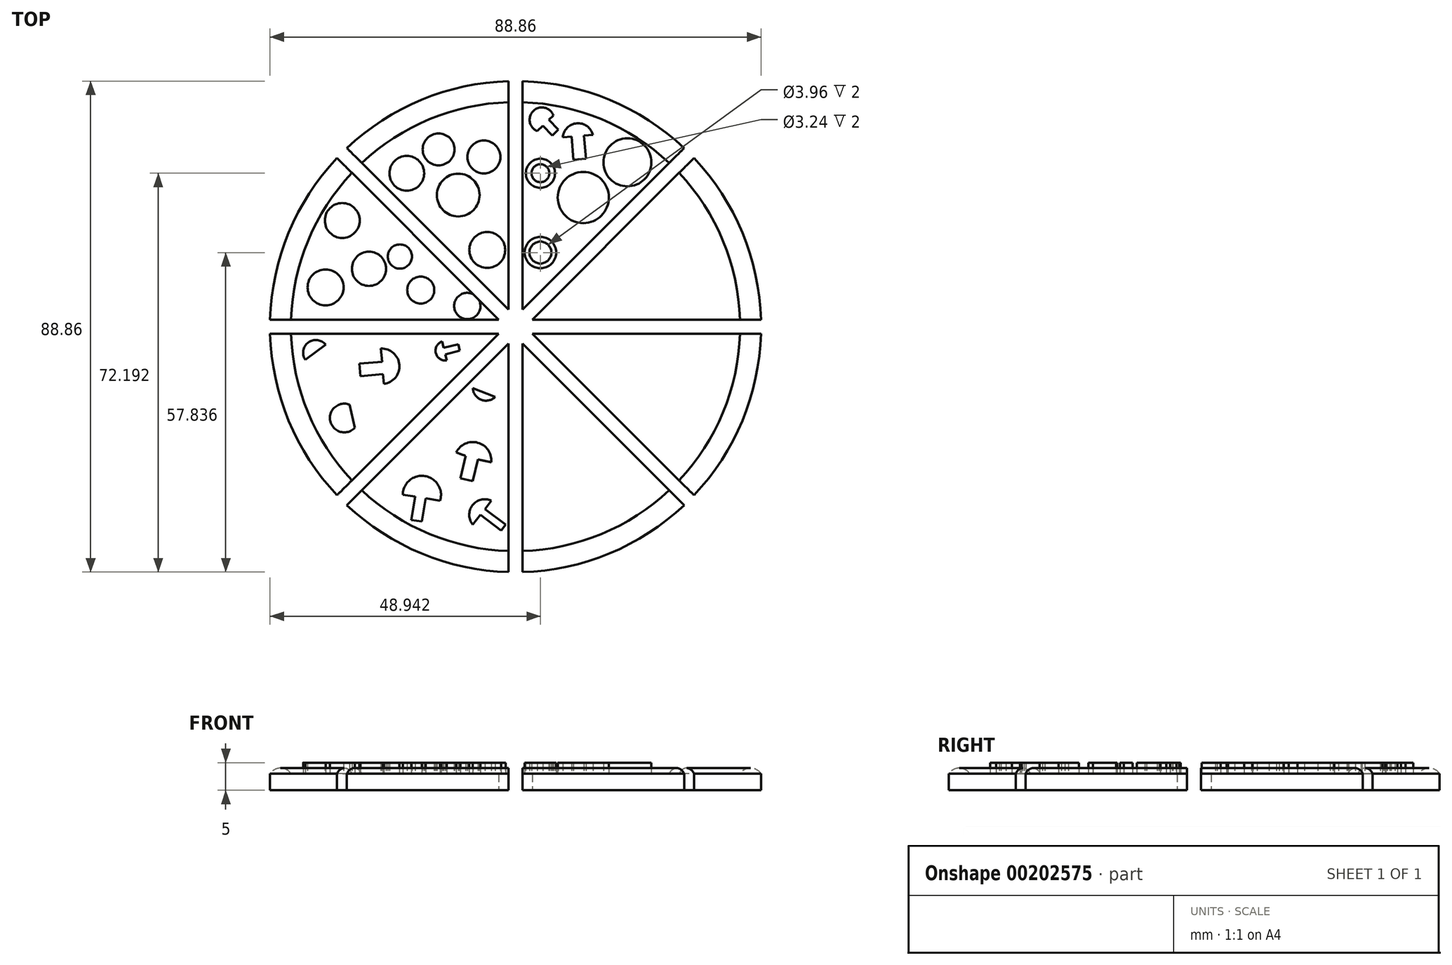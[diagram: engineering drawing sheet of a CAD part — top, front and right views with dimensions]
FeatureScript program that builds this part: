
annotation { "Feature Type Name" : "Feature", "Feature Type Description" : "" }
export const myFeature = defineFeature(function(context is Context, id is Id, definition is map)
    precondition{}
    {
        {
            var Q0;
            Q0=qCreatedBy(makeId("Top.planeOp"),FACE);
            var sketch = newSketch(context, id + "F0", { "sketchPlane" : qUnion([Q0])});
            skCircle(sketch, "E0", {"center": v(0, 0) * mm, "radius": 44.45 * mm});
            skSolve(sketch);
        }
        {
            var Q0;
            Q0 = qSketchRegion(id + "F0", true);
            extrude(context, id + "F1", {"entities" : qUnion([Q0]), "depth" : 2 * mm});
        }
        {
            var Q0;
            Q0=makeQuery(id+"F1.opExtrude","CAP_FACE",FACE,{"disambiguationData":[OSD([sQuery(id+"F0.wireOp",EDGE,"E0")])],"isStart":false});
            var sketch = newSketch(context, id + "F2", { "sketchPlane" : qUnion([Q0])});
            skLineSegment(sketch, "E1", {"start": v(0, 0) * mm, "end": v(0, 44.45) * mm});
            skLineSegment(sketch, "E2", {"start": v(0, 44.45) * mm, "end": v(0, -44.45) * mm});
            skLineSegment(sketch, "E3", {"start": v(0, -44.45) * mm, "end": v(0, 0) * mm});
            skLineSegment(sketch, "E4", {"start": v(0, 0) * mm, "end": v(-44.45, 0) * mm});
            skLineSegment(sketch, "E5", {"start": v(0, 0) * mm, "end": v(44.45, 0) * mm});
            skLineSegment(sketch, "E6", {"start": v(0, 0) * mm, "end": v(-31.43, -31.43) * mm});
            skLineSegment(sketch, "E7", {"start": v(-31.43, -31.43) * mm, "end": v(31.43, 31.43) * mm});
            skLineSegment(sketch, "E8", {"start": v(31.43, 31.43) * mm, "end": v(0, 0) * mm});
            skLineSegment(sketch, "E9", {"start": v(0, 0) * mm, "end": v(-31.43, 31.43) * mm});
            skLineSegment(sketch, "E10", {"start": v(0, 0) * mm, "end": v(31.43, -31.43) * mm});
            skSolve(sketch);
        }
        {
            var Q0;
            {var subQ0=sQuery(id+"F2.wireOp",EDGE,"E4");Q0=makeQuery(id+"F2.imprint","IMPRINT",FACE,{"disambiguationData":[TD([[makeQuery(id+"F2.imprint","IMPRINT",EDGE,{"derivedFrom":subQ0}),-1.0]])]});}
            var sketch = newSketch(context, id + "F3", { "sketchPlane" : qUnion([Q0])});
            skCircle(sketch, "E11", {"center": v(-17.15, 6.62) * mm, "radius": 2.44 * mm});
            skCircle(sketch, "E12", {"center": v(-26.52, 10.46) * mm, "radius": 3.1 * mm});
            skCircle(sketch, "E13", {"center": v(-34.38, 7.1) * mm, "radius": 3.26 * mm});
            skCircle(sketch, "E14", {"center": v(-31.36, 19.2) * mm, "radius": 3.15 * mm});
            skCircle(sketch, "E15", {"center": v(-20.94, 12.69) * mm, "radius": 2.19 * mm});
            skCircle(sketch, "E16", {"center": v(-8.72, 3.73) * mm, "radius": 2.38 * mm});
            skCircle(sketch, "E17", {"center": v(-5.1, 13.87) * mm, "radius": 3.25 * mm});
            skCircle(sketch, "E18", {"center": v(-10.37, 23.81) * mm, "radius": 3.87 * mm});
            skCircle(sketch, "E19", {"center": v(-19.68, 27.75) * mm, "radius": 3.14 * mm});
            skCircle(sketch, "E20", {"center": v(-5.73, 30.7) * mm, "radius": 2.98 * mm});
            skCircle(sketch, "E21", {"center": v(-13.92, 32.07) * mm, "radius": 2.88 * mm});
            skArc(sketch, "E22", {"start": v(-23.83, -10.37) * mm, "mid": v(-21.02, -6.92) * mm, "end": v(-24.36, -3.96) * mm});
            skLineSegment(sketch, "E23", {"start": v(-24.36, -3.96) * mm, "end": v(-23.83, -10.37) * mm});
            skLineSegment(sketch, "E24", {"start": v(-24.16, -6.4) * mm, "end": v(-28.23, -6.72) * mm});
            skLineSegment(sketch, "E25", {"start": v(-28.23, -6.72) * mm, "end": v(-28.04, -8.95) * mm});
            skLineSegment(sketch, "E26", {"start": v(-28.04, -8.95) * mm, "end": v(-23.83, -8.6) * mm});
            skArc(sketch, "E27", {"start": v(-30.03, -14.12) * mm, "mid": v(-33.53, -17.1) * mm, "end": v(-29.1, -18.34) * mm});
            skLineSegment(sketch, "E28", {"start": v(-30.03, -14.12) * mm, "end": v(-29.1, -18.34) * mm});
            skLineSegment(sketch, "E29", {"start": v(-29.75, -15.36) * mm, "end": v(-25.7, -14.84) * mm});
            skLineSegment(sketch, "E30", {"start": v(-25.66, -14.89) * mm, "end": v(-25.23, -16.85) * mm});
            skLineSegment(sketch, "E31", {"start": v(-25.28, -16.74) * mm, "end": v(-29.34, -17.23) * mm});
            skArc(sketch, "E32", {"start": v(-34.35, -3.28) * mm, "mid": v(-37.5, -2.87) * mm, "end": v(-38.06, -6) * mm});
            skLineSegment(sketch, "E33", {"start": v(-34.35, -3.28) * mm, "end": v(-38.06, -6) * mm});
            skLineSegment(sketch, "E34", {"start": v(-36.8, -5.08) * mm, "end": v(-34.95, -7.6) * mm});
            skLineSegment(sketch, "E35", {"start": v(-34.82, -7.51) * mm, "end": v(-33.5, -6.54) * mm});
            skLineSegment(sketch, "E36", {"start": v(-33.5, -6.54) * mm, "end": v(-35.34, -4) * mm});
            skArc(sketch, "E37", {"start": v(-13.29, -2.68) * mm, "mid": v(-14.42, -4.8) * mm, "end": v(-12.41, -6.13) * mm});
            skLineSegment(sketch, "E38", {"start": v(-13.29, -2.68) * mm, "end": v(-12.41, -6.13) * mm});
            skLineSegment(sketch, "E39", {"start": v(-13, -3.86) * mm, "end": v(-10.36, -3.19) * mm});
            skLineSegment(sketch, "E40", {"start": v(-10.36, -3.19) * mm, "end": v(-10.06, -4.36) * mm});
            skLineSegment(sketch, "E41", {"start": v(-10.06, -4.36) * mm, "end": v(-12.7, -5.03) * mm});
            skArc(sketch, "E42", {"start": v(-4.4, -24.53) * mm, "mid": v(-6.83, -21.01) * mm, "end": v(-10.73, -22.77) * mm});
            skArc(sketch, "E43", {"start": v(-10.73, -22.77) * mm, "mid": v(-7.61, -23.82) * mm, "end": v(-4.4, -24.53) * mm});
            skLineSegment(sketch, "E44", {"start": v(-9, -23.4) * mm, "end": v(-9.95, -27.47) * mm});
            skLineSegment(sketch, "E45", {"start": v(-9.95, -27.47) * mm, "end": v(-7.73, -28) * mm});
            skLineSegment(sketch, "E46", {"start": v(-7.73, -28) * mm, "end": v(-6.8, -24.04) * mm});
            skArc(sketch, "E47", {"start": v(-13.64, -31.5) * mm, "mid": v(-16.4, -27.05) * mm, "end": v(-20.4, -30.44) * mm});
            skArc(sketch, "E48", {"start": v(-7.73, -11.15) * mm, "mid": v(-6.22, -13.24) * mm, "end": v(-3.7, -12.75) * mm});
            skArc(sketch, "E49", {"start": v(-4.4, -31.5) * mm, "mid": v(-7.8, -32.36) * mm, "end": v(-7.73, -35.87) * mm});
            skLineSegment(sketch, "E50", {"start": v(-20.4, -30.44) * mm, "end": v(-13.64, -31.5) * mm});
            skLineSegment(sketch, "E51", {"start": v(-18.18, -30.79) * mm, "end": v(-18.84, -34.99) * mm});
            skLineSegment(sketch, "E52", {"start": v(-18.84, -34.99) * mm, "end": v(-16.94, -35.28) * mm});
            skLineSegment(sketch, "E53", {"start": v(-16.94, -35.28) * mm, "end": v(-16.19, -30.46) * mm});
            skLineSegment(sketch, "E54", {"start": v(-4.4, -31.5) * mm, "end": v(-7.73, -35.87) * mm});
            skLineSegment(sketch, "E55", {"start": v(-6.36, -34.07) * mm, "end": v(-2.6, -36.92) * mm});
            skLineSegment(sketch, "E56", {"start": v(-2.6, -36.92) * mm, "end": v(-1.8, -35.87) * mm});
            skLineSegment(sketch, "E57", {"start": v(-1.8, -35.87) * mm, "end": v(-5.56, -33.02) * mm});
            skLineSegment(sketch, "E58", {"start": v(-7.73, -11.15) * mm, "end": v(-3.7, -12.75) * mm});
            skLineSegment(sketch, "E59", {"start": v(-6.45, -11.66) * mm, "end": v(-5.48, -9.22) * mm});
            skLineSegment(sketch, "E60", {"start": v(-5.48, -9.22) * mm, "end": v(-4.4, -9.64) * mm});
            skLineSegment(sketch, "E61", {"start": v(-4.4, -9.64) * mm, "end": v(-5.34, -12.02) * mm});
            skSolve(sketch);
        }
        {
            var Q0;
            {var subQ0=sQuery(id+"F2.wireOp",EDGE,"E3");Q0=makeQuery(id+"F2.imprint","IMPRINT",FACE,{"disambiguationData":[TD([[makeQuery(id+"F2.imprint","IMPRINT",EDGE,{"derivedFrom":subQ0}),-1.0]])]});}
            var sketch = newSketch(context, id + "F4", { "sketchPlane" : qUnion([Q0])});
            skCircle(sketch, "E62", {"center": v(6.9, -18.48) * mm, "radius": 2.53 * mm});
            skCircle(sketch, "E63", {"center": v(6.9, -18.48) * mm, "radius": 1.2 * mm});
            skCircle(sketch, "E64", {"center": v(14.78, -26.64) * mm, "radius": 2.58 * mm});
            skCircle(sketch, "E65", {"center": v(14.78, -26.64) * mm, "radius": 1.15 * mm});
            skCircle(sketch, "E66", {"center": v(6.9, -29.82) * mm, "radius": 3 * mm});
            skCircle(sketch, "E67", {"center": v(6.9, -29.82) * mm, "radius": 1.7 * mm});
            skCircle(sketch, "E68", {"center": v(3.81, -10.2) * mm, "radius": 2.25 * mm});
            skCircle(sketch, "E69", {"center": v(3.81, -10.2) * mm, "radius": 1.02 * mm});
            skCircle(sketch, "E70", {"center": v(14.78, -21.52) * mm, "radius": 1.92 * mm});
            skCircle(sketch, "E71", {"center": v(14.78, -21.52) * mm, "radius": 1.04 * mm});
            skCircle(sketch, "E72", {"center": v(8.02, -24.24) * mm, "radius": 1.63 * mm});
            skCircle(sketch, "E73", {"center": v(8.02, -24.24) * mm, "radius": 0.76 * mm});
            skCircle(sketch, "E74", {"center": v(9.02, -13.81) * mm, "radius": 1.57 * mm});
            skCircle(sketch, "E75", {"center": v(9.02, -13.81) * mm, "radius": 0.77 * mm});
            skCircle(sketch, "E76", {"center": v(20.39, -29.82) * mm, "radius": 2 * mm});
            skCircle(sketch, "E77", {"center": v(20.39, -29.82) * mm, "radius": 0.9 * mm});
            skCircle(sketch, "E78", {"center": v(14.17, -32.94) * mm, "radius": 1.74 * mm});
            skCircle(sketch, "E79", {"center": v(14.17, -32.94) * mm, "radius": 1.03 * mm});
            skCircle(sketch, "E80", {"center": v(12.24, -17.99) * mm, "radius": 1.33 * mm});
            skCircle(sketch, "E81", {"center": v(12.24, -17.99) * mm, "radius": 0.68 * mm});
            skCircle(sketch, "E82", {"center": v(3.21, -23.56) * mm, "radius": 1.84 * mm});
            skCircle(sketch, "E83", {"center": v(3.21, -23.56) * mm, "radius": 1.07 * mm});
            skCircle(sketch, "E84", {"center": v(3.21, -15.6) * mm, "radius": 1.18 * mm});
            skCircle(sketch, "E85", {"center": v(3.21, -15.6) * mm, "radius": 0.77 * mm});
            skCircle(sketch, "E86", {"center": v(10.88, -4.09) * mm, "radius": 2.02 * mm});
            skCircle(sketch, "E87", {"center": v(10.88, -4.09) * mm, "radius": 1.15 * mm});
            skCircle(sketch, "E88", {"center": v(16.31, -9.98) * mm, "radius": 1.71 * mm});
            skCircle(sketch, "E89", {"center": v(16.31, -9.98) * mm, "radius": 0.83 * mm});
            skCircle(sketch, "E90", {"center": v(16.96, -5.53) * mm, "radius": 2.08 * mm});
            skCircle(sketch, "E91", {"center": v(16.96, -5.53) * mm, "radius": 1.15 * mm});
            skCircle(sketch, "E92", {"center": v(23.55, -9.06) * mm, "radius": 2.22 * mm});
            skCircle(sketch, "E93", {"center": v(23.55, -9.06) * mm, "radius": 1.36 * mm});
            skCircle(sketch, "E94", {"center": v(23.55, -16.64) * mm, "radius": 2.05 * mm});
            skCircle(sketch, "E95", {"center": v(23.55, -16.64) * mm, "radius": 0.93 * mm});
            skCircle(sketch, "E96", {"center": v(19.28, -13.99) * mm, "radius": 1.5 * mm});
            skCircle(sketch, "E97", {"center": v(19.28, -13.99) * mm, "radius": 0.9 * mm});
            skCircle(sketch, "E98", {"center": v(27.46, -4.86) * mm, "radius": 1.79 * mm});
            skCircle(sketch, "E99", {"center": v(27.46, -4.86) * mm, "radius": 1.17 * mm});
            skCircle(sketch, "E100", {"center": v(30.72, -12.47) * mm, "radius": 2.18 * mm});
            skCircle(sketch, "E101", {"center": v(30.72, -12.47) * mm, "radius": 1.22 * mm});
            skCircle(sketch, "E102", {"center": v(34.59, -7.21) * mm, "radius": 1.92 * mm});
            skCircle(sketch, "E103", {"center": v(34.59, -7.21) * mm, "radius": 0.87 * mm});
            skCircle(sketch, "E104", {"center": v(29.25, -21.24) * mm, "radius": 2.7 * mm});
            skCircle(sketch, "E105", {"center": v(29.25, -21.24) * mm, "radius": 1.86 * mm});
            skCircle(sketch, "E106", {"center": v(22.12, -3.09) * mm, "radius": 1.8 * mm});
            skCircle(sketch, "E107", {"center": v(22.12, -3.09) * mm, "radius": 0.9 * mm});
            skSolve(sketch);
        }
        {
            var Q0;
            {var subQ0=sQuery(id+"F2.wireOp",EDGE,"E2");Q0=makeQuery(id+"F2.imprint","IMPRINT",FACE,{"disambiguationData":[TD([[makeQuery(id+"F2.imprint","IMPRINT",EDGE,{"derivedFrom":subQ0}),1.0]])]});}
            var sketch = newSketch(context, id + "F5", { "sketchPlane" : qUnion([Q0])});
            skCircle(sketch, "E108", {"center": v(12.27, 23.36) * mm, "radius": 4.63 * mm});
            skCircle(sketch, "E109", {"center": v(4.51, 13.4) * mm, "radius": 2.85 * mm});
            skCircle(sketch, "E110", {"center": v(4.51, 13.4) * mm, "radius": 1.98 * mm});
            skCircle(sketch, "E111", {"center": v(20.26, 29.73) * mm, "radius": 4.34 * mm});
            skCircle(sketch, "E112", {"center": v(4.51, 27.76) * mm, "radius": 2.64 * mm});
            skCircle(sketch, "E113", {"center": v(4.51, 27.76) * mm, "radius": 1.62 * mm});
            skArc(sketch, "E114", {"start": v(14, 34.7) * mm, "mid": v(11.09, 36.8) * mm, "end": v(8.56, 34.24) * mm});
            skPoint(sketch, "E115.endSnap0", {"position": v(11.09, 36.8) * mm});
            skLineSegment(sketch, "E116", {"start": v(8.56, 34.24) * mm, "end": v(14, 34.7) * mm});
            skLineSegment(sketch, "E117", {"start": v(10.14, 34.38) * mm, "end": v(10.5, 30.19) * mm});
            skLineSegment(sketch, "E118", {"start": v(10.5, 30.19) * mm, "end": v(12.74, 30.38) * mm});
            skLineSegment(sketch, "E119", {"start": v(12.74, 30.38) * mm, "end": v(12.37, 34.7) * mm});
            skArc(sketch, "E120", {"start": v(6.85, 38.24) * mm, "mid": v(3.24, 39.05) * mm, "end": v(3.92, 35.4) * mm});
            skLineSegment(sketch, "E121", {"start": v(6.85, 38.24) * mm, "end": v(3.92, 35.4) * mm});
            skLineSegment(sketch, "E122", {"start": v(6.05, 37.46) * mm, "end": v(7.78, 35.66) * mm});
            skLineSegment(sketch, "E123", {"start": v(7.78, 35.66) * mm, "end": v(6.66, 34.58) * mm});
            skLineSegment(sketch, "E124", {"start": v(6.66, 34.58) * mm, "end": v(4.93, 36.38) * mm});
            skSolve(sketch);
        }
        {
            var Q0;
            Q0 = qSketchRegion(id + "F3", true);
            var Q1;
            Q1 = qSketchRegion(id + "F4", true);
            var Q2;
            Q2 = qSketchRegion(id + "F5", true);
            extrude(context, id + "F6", {"entities" : qUnion([Q0, Q1, Q2]), "operationType" : NewBodyOperationType.ADD, "depth" : 2 * mm});
        }
        {
            var Q0;
            Q0=makeQuery(id+"F1.opExtrude","CAP_FACE",FACE,{"disambiguationData":[OSD([sQuery(id+"F0.wireOp",EDGE,"E0")])],"isStart":true});
            extrude(context, id + "F7", {"entities" : qUnion([Q0]), "operationType" : NewBodyOperationType.ADD, "depth" : 1 * mm});
        }
        {
            var Q0;
            Q0=qCreatedBy(makeId("Front.planeOp"),FACE);
            var sketch = newSketch(context, id + "F8", { "sketchPlane" : qUnion([Q0])});
            skArc(sketch, "E125", {"start": v(44.45, 2) * mm, "mid": v(42.55, 3.02) * mm, "end": v(40.64, 2) * mm});
            skLineSegment(sketch, "E126", {"start": v(44.45, 2) * mm, "end": v(40.64, 2) * mm});
            skSolve(sketch);
        }
        {
            var Q0;
            Q0=makeQuery(id+"F8.imprint","IMPRINT",FACE,{"disambiguationData":[TD([[makeQuery(id+"F8.imprint","IMPRINT",EDGE,{"derivedFrom":sQuery(id+"F8.wireOp",EDGE,"E125")}),1.0]])]});
            var Q1;
            Q1 = qConstructionFilter(qBodyType(qCreatedBy(id + "F0" ,EDGE), BodyType.WIRE), ConstructionObject.NO);
            sweep(context, id + "F9", {"operationType" : NewBodyOperationType.ADD, "profiles" : qUnion([Q0]), "path" : qUnion([Q1])});
        }
        {
            var Q0;
            Q0=makeQuery(id+"F7.opExtrude","CAP_FACE",FACE,{"disambiguationData":[OSD([sQuery(id+"F0.wireOp",EDGE,"E0")])],"isStart":false});
            var sketch = newSketch(context, id + "F10", { "sketchPlane" : qUnion([Q0])});
            skLineSegment(sketch, "E127.bottom", {"start": v(-1.27, 44.45) * mm, "end": v(1.27, 44.45) * mm});
            skLineSegment(sketch, "E127.top", {"start": v(-1.27, -44.45) * mm, "end": v(1.27, -44.45) * mm});
            skLineSegment(sketch, "E127.left", {"start": v(-1.27, 44.45) * mm, "end": v(-1.27, -44.45) * mm});
            skLineSegment(sketch, "E127.right", {"start": v(1.27, 44.45) * mm, "end": v(1.27, -44.45) * mm});
            skPoint(sketch, "E127.middle", {"position": v(0, 0) * mm});
            skLineSegment(sketch, "E128.bottom", {"start": v(-44.45, 1.27) * mm, "end": v(44.45, 1.27) * mm});
            skLineSegment(sketch, "E128.top", {"start": v(-44.45, -1.27) * mm, "end": v(44.45, -1.27) * mm});
            skLineSegment(sketch, "E128.left", {"start": v(-44.45, 1.27) * mm, "end": v(-44.45, -1.27) * mm});
            skLineSegment(sketch, "E128.right", {"start": v(44.45, 1.27) * mm, "end": v(44.45, -1.27) * mm});
            skLineSegment(sketch, "E129", {"start": v(0, 0) * mm, "end": v(-31.43, 31.43) * mm});
            skLineSegment(sketch, "E130", {"start": v(0, 0) * mm, "end": v(-31.43, -31.43) * mm});
            skLineSegment(sketch, "E131", {"start": v(0, 0) * mm, "end": v(-0.9, -0.9) * mm});
            skLineSegment(sketch, "E132", {"start": v(-0.9, -0.9) * mm, "end": v(-32.33, 30.53) * mm});
            skLineSegment(sketch, "E133", {"start": v(-32.33, 30.53) * mm, "end": v(-30.53, 32.33) * mm});
            skLineSegment(sketch, "E134", {"start": v(-30.53, 32.33) * mm, "end": v(0.9, 0.9) * mm});
            skLineSegment(sketch, "E135", {"start": v(0.9, 0.9) * mm, "end": v(0, 0) * mm});
            skLineSegment(sketch, "E136", {"start": v(0.9, 0.9) * mm, "end": v(32.33, -30.53) * mm});
            skLineSegment(sketch, "E137", {"start": v(32.33, -30.53) * mm, "end": v(0.9, 0.9) * mm});
            skLineSegment(sketch, "E138", {"start": v(-0.9, -0.9) * mm, "end": v(30.53, -32.33) * mm});
            skLineSegment(sketch, "E139", {"start": v(30.53, -32.33) * mm, "end": v(32.33, -30.53) * mm});
            skLineSegment(sketch, "E140.MirrorCS", {"start": v(30.53, 32.33) * mm, "end": v(-0.9, 0.9) * mm});
            skLineSegment(sketch, "E141.MirrorCS", {"start": v(0.9, -0.9) * mm, "end": v(32.33, 30.53) * mm});
            skLineSegment(sketch, "E142.MirrorCS", {"start": v(-32.33, -30.53) * mm, "end": v(-0.9, 0.9) * mm});
            skLineSegment(sketch, "E143.MirrorCS", {"start": v(0.9, -0.9) * mm, "end": v(-30.53, -32.33) * mm});
            skLineSegment(sketch, "E144", {"start": v(30.53, 32.33) * mm, "end": v(32.33, 30.53) * mm});
            skLineSegment(sketch, "E145", {"start": v(-30.53, -32.33) * mm, "end": v(-32.33, -30.53) * mm});
            skCircle(sketch, "E146", {"center": v(0, 0) * mm, "radius": 2.54 * mm});
            skSolve(sketch);
        }
        {
            var Q0;
            Q0 = qSketchRegion(id + "F10", true);
            extrude(context, id + "F11", {"entities" : qUnion([Q0]), "operationType" : NewBodyOperationType.REMOVE, "endBound" : BoundingType.THROUGH_ALL, "oppositeDirection" : true, "depth" : 25.4 * mm});
        }
        {
            var Q0;
            {var subQ0=sQuery(id+"F2.wireOp",EDGE,"E2");Q0=makeQuery(id+"F2.imprint","IMPRINT",FACE,{"disambiguationData":[TD([[makeQuery(id+"F2.imprint","IMPRINT",EDGE,{"derivedFrom":subQ0}),-1.0]])]});}
            var sketch = newSketch(context, id + "F12", { "sketchPlane" : qUnion([Q0])});
            skCircle(sketch, "E147", {"center": v(0, 0) * mm, "radius": 2.54 * mm});
            skSolve(sketch);
        }
        {
            var Q0;
            Q0 = qSketchRegion(id + "F12", true);
            extrude(context, id + "F13", {"entities" : qUnion([Q0]), "operationType" : NewBodyOperationType.REMOVE, "endBound" : BoundingType.THROUGH_ALL, "oppositeDirection" : true, "depth" : 25.4 * mm});
        }
    });
